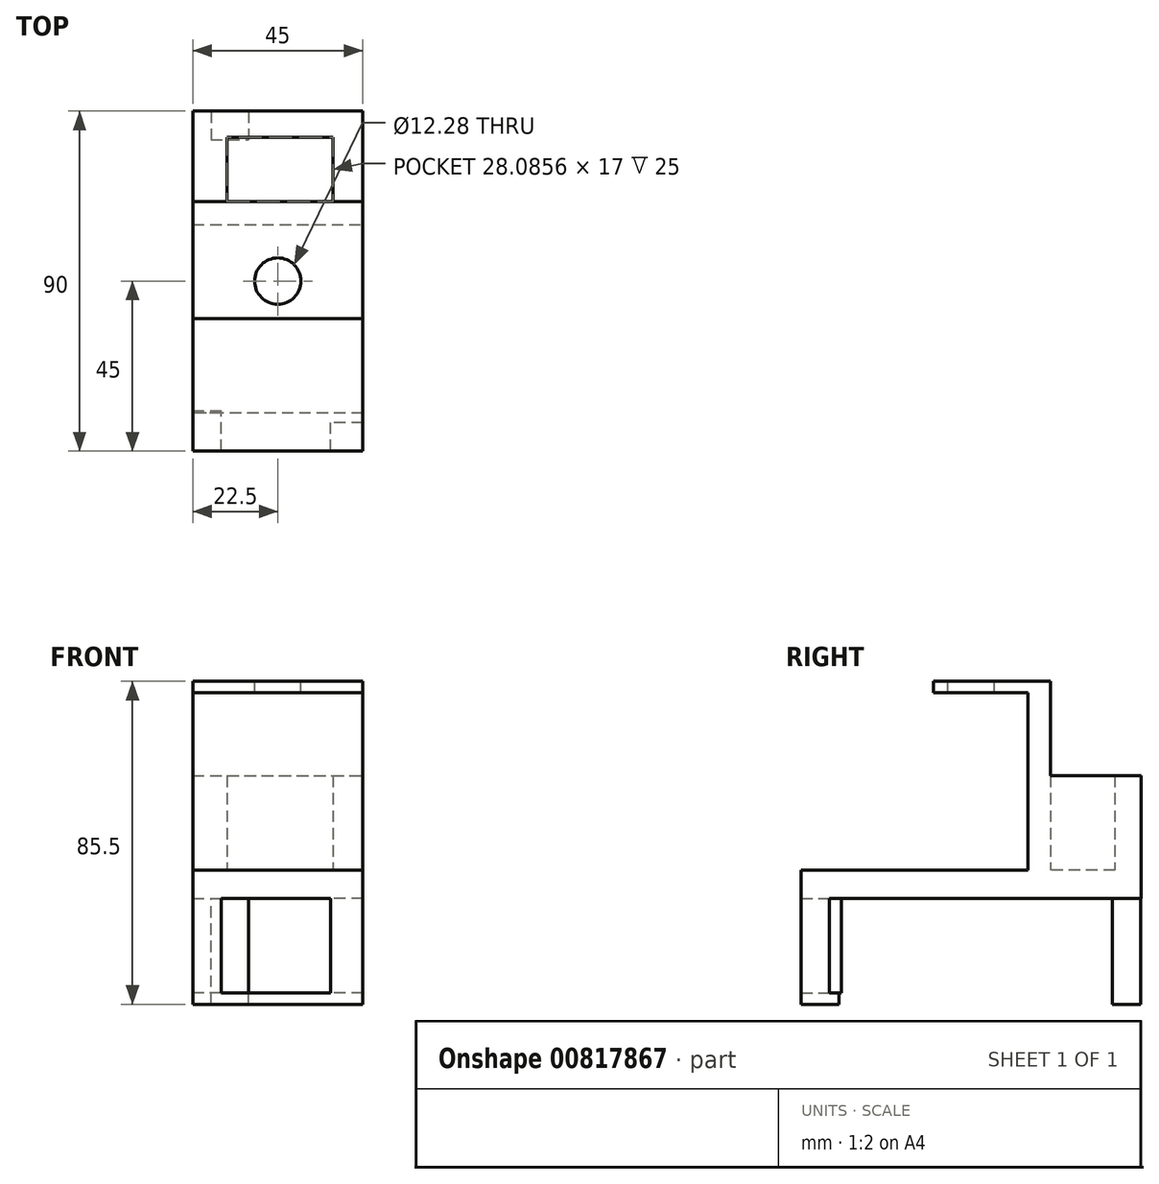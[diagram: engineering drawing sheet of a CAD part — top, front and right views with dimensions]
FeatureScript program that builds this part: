
annotation { "Feature Type Name" : "Feature", "Feature Type Description" : "" }
export const myFeature = defineFeature(function(context is Context, id is Id, definition is map)
    precondition{}
    {
        {
            var Q0;
            Q0=qCreatedBy(makeId("Top.planeOp"),FACE);
            var sketch = newSketch(context, id + "F0", { "sketchPlane" : qUnion([Q0])});
            skLineSegment(sketch, "E0.bottom", {"start": v(-22.5, 45) * mm, "end": v(22.5, 45) * mm});
            skLineSegment(sketch, "E0.top", {"start": v(-22.5, -45) * mm, "end": v(22.5, -45) * mm});
            skLineSegment(sketch, "E0.left", {"start": v(-22.5, 45) * mm, "end": v(-22.5, -45) * mm});
            skLineSegment(sketch, "E0.right", {"start": v(22.5, 45) * mm, "end": v(22.5, -45) * mm});
            skPoint(sketch, "E0.middle", {"position": v(0, 0) * mm});
            skSolve(sketch);
        }
        {
            var Q0;
            Q0=makeQuery(id+"F0.imprint","IMPRINT",FACE,{"disambiguationData":[TD([[makeQuery(id+"F0.imprint","IMPRINT",EDGE,{"derivedFrom":sQuery(id+"F0.wireOp",EDGE,"E0.bottom")}),-1.0]])]});
            extrude(context, id + "F1", {"entities" : qUnion([Q0]), "depth" : 7.5 * mm, "offsetDistance" : 25 * mm});
        }
        {
            var Q0;
            Q0=makeQuery(id+"F1.opExtrude","CAP_FACE",FACE,{"disambiguationData":[OSD([sQuery(id+"F0.wireOp",EDGE,"E0.bottom"),sQuery(id+"F0.wireOp",EDGE,"E0.top"),sQuery(id+"F0.wireOp",EDGE,"E0.left"),sQuery(id+"F0.wireOp",EDGE,"E0.right")])],"isStart":false});
            var sketch = newSketch(context, id + "F2", { "sketchPlane" : qUnion([Q0])});
            skLineSegment(sketch, "E1.bottom", {"start": v(-22.5, 45) * mm, "end": v(22.5, 45) * mm});
            skLineSegment(sketch, "E1.top", {"start": v(-22.5, 15) * mm, "end": v(22.5, 15) * mm});
            skLineSegment(sketch, "E1.left", {"start": v(-22.5, 45) * mm, "end": v(-22.5, 15) * mm});
            skLineSegment(sketch, "E1.right", {"start": v(22.5, 45) * mm, "end": v(22.5, 15) * mm});
            skLineSegment(sketch, "E2.bottom", {"start": v(-13.5, 38.06) * mm, "end": v(14.6, 38.06) * mm});
            skLineSegment(sketch, "E2.top", {"start": v(-13.5, 21.06) * mm, "end": v(14.6, 21.06) * mm});
            skLineSegment(sketch, "E2.left", {"start": v(-13.5, 38.06) * mm, "end": v(-13.5, 21.06) * mm});
            skLineSegment(sketch, "E2.right", {"start": v(14.6, 38.06) * mm, "end": v(14.6, 21.06) * mm});
            skSolve(sketch);
        }
        {
            var Q0;
            Q0=makeQuery(id+"F2.imprint","IMPRINT",FACE,{"disambiguationData":[TD([[makeQuery(id+"F2.imprint","IMPRINT",EDGE,{"derivedFrom":sQuery(id+"F2.wireOp",EDGE,"E1.bottom")}),-1.0]])]});
            extrude(context, id + "F3", {"entities" : qUnion([Q0]), "operationType" : NewBodyOperationType.ADD, "depth" : 25 * mm, "offsetDistance" : 25 * mm});
        }
        {
            var Q0;
            Q0=makeQuery(id+"F3.opExtrude","CAP_FACE",FACE,{"disambiguationData":[OSD([sQuery(id+"F2.wireOp",EDGE,"E1.bottom"),sQuery(id+"F2.wireOp",EDGE,"E1.top"),sQuery(id+"F2.wireOp",EDGE,"E1.left"),sQuery(id+"F2.wireOp",EDGE,"E1.right"),sQuery(id+"F2.wireOp",EDGE,"E2.bottom"),sQuery(id+"F2.wireOp",EDGE,"E2.top"),sQuery(id+"F2.wireOp",EDGE,"E2.left"),sQuery(id+"F2.wireOp",EDGE,"E2.right")])],"isStart":false});
            var sketch = newSketch(context, id + "F4", { "sketchPlane" : qUnion([Q0])});
            skLineSegment(sketch, "E3.bottom", {"start": v(22.5, 15) * mm, "end": v(-22.5, 15) * mm});
            skLineSegment(sketch, "E3.top", {"start": v(22.5, 21.06) * mm, "end": v(-22.5, 21.06) * mm});
            skLineSegment(sketch, "E3.left", {"start": v(22.5, 15) * mm, "end": v(22.5, 21.06) * mm});
            skLineSegment(sketch, "E3.right", {"start": v(-22.5, 15) * mm, "end": v(-22.5, 21.06) * mm});
            skSolve(sketch);
        }
        {
            var Q0;
            Q0=makeQuery(id+"F4.imprint","IMPRINT",FACE,{"disambiguationData":[TD([[makeQuery(id+"F4.imprint","IMPRINT",EDGE,{"derivedFrom":sQuery(id+"F4.wireOp",EDGE,"E3.bottom")}),1.0]])]});
            extrude(context, id + "F5", {"entities" : qUnion([Q0]), "operationType" : NewBodyOperationType.ADD, "depth" : 25 * mm, "offsetDistance" : 25 * mm});
        }
        {
            var Q0;
            Q0=makeQuery(id+"F5.boolean.opBoolean","MERGE",FACE,{"derivedFrom":[makeQuery(id+"F3.opExtrude","SWEPT_FACE",FACE,{"disambiguationData":[OSD([sQuery(id+"F2.wireOp",EDGE,"E1.top")])]}),makeQuery(id+"F5.opExtrude","SWEPT_FACE",FACE,{"disambiguationData":[OSD([sQuery(id+"F4.wireOp",EDGE,"E3.bottom")])]})]});
            var sketch = newSketch(context, id + "F6", { "sketchPlane" : qUnion([Q0])});
            skLineSegment(sketch, "E4.bottom", {"start": v(-22.5, 57.5) * mm, "end": v(22.5, 57.5) * mm});
            skLineSegment(sketch, "E4.top", {"start": v(-22.5, 54.5) * mm, "end": v(22.5, 54.5) * mm});
            skLineSegment(sketch, "E4.left", {"start": v(-22.5, 57.5) * mm, "end": v(-22.5, 54.5) * mm});
            skLineSegment(sketch, "E4.right", {"start": v(22.5, 57.5) * mm, "end": v(22.5, 54.5) * mm});
            skSolve(sketch);
        }
        {
            var Q0;
            Q0=makeQuery(id+"F6.imprint","IMPRINT",FACE,{"disambiguationData":[TD([[makeQuery(id+"F6.imprint","IMPRINT",EDGE,{"derivedFrom":sQuery(id+"F6.wireOp",EDGE,"E4.bottom")}),-1.0]])]});
            extrude(context, id + "F7", {"entities" : qUnion([Q0]), "operationType" : NewBodyOperationType.ADD, "depth" : 25 * mm, "offsetDistance" : 25 * mm});
        }
        {
            var Q0;
            Q0=makeQuery(id+"F7.boolean.opBoolean","MERGE",FACE,{"derivedFrom":[makeQuery(id+"F5.opExtrude","CAP_FACE",FACE,{"disambiguationData":[OSD([sQuery(id+"F4.wireOp",EDGE,"E3.bottom"),sQuery(id+"F4.wireOp",EDGE,"E3.top"),sQuery(id+"F4.wireOp",EDGE,"E3.left"),sQuery(id+"F4.wireOp",EDGE,"E3.right")])],"isStart":false}),makeQuery(id+"F7.opExtrude","SWEPT_FACE",FACE,{"disambiguationData":[OSD([sQuery(id+"F6.wireOp",EDGE,"E4.bottom")])]})]});
            var sketch = newSketch(context, id + "F8", { "sketchPlane" : qUnion([Q0])});
            skCircle(sketch, "E5", {"center": v(0, 0) * mm, "radius": 6.14 * mm});
            skSolve(sketch);
        }
        {
            var Q0;
            Q0=makeQuery(id+"F8.imprint","IMPRINT",FACE,{"disambiguationData":[TD([[makeQuery(id+"F8.imprint","IMPRINT",EDGE,{"derivedFrom":sQuery(id+"F8.wireOp",EDGE,"E5")}),1.0]])]});
            var Q1;
            Q1=sQuery(id+"F8.wireOp",EDGE,"E5");
            extrude(context, id + "F9", {"entities" : qUnion([Q0]), "operationType" : NewBodyOperationType.REMOVE, "surfaceEntities" : qUnion([Q1]), "endBound" : BoundingType.UP_TO_NEXT, "oppositeDirection" : true, "depth" : 25 * mm, "offsetDistance" : 25 * mm});
        }
        {
            var Q0;
            Q0=makeQuery(id+"F1.opExtrude","CAP_FACE",FACE,{"disambiguationData":[OSD([sQuery(id+"F0.wireOp",EDGE,"E0.bottom"),sQuery(id+"F0.wireOp",EDGE,"E0.top"),sQuery(id+"F0.wireOp",EDGE,"E0.left"),sQuery(id+"F0.wireOp",EDGE,"E0.right")])],"isStart":true});
            var sketch = newSketch(context, id + "F10", { "sketchPlane" : qUnion([Q0])});
            skLineSegment(sketch, "E6.bottom", {"start": v(22.5, 45) * mm, "end": v(14, 45) * mm});
            skLineSegment(sketch, "E6.top", {"start": v(22.5, 37.5) * mm, "end": v(14, 37.5) * mm});
            skLineSegment(sketch, "E6.left", {"start": v(22.5, 45) * mm, "end": v(22.5, 37.5) * mm});
            skLineSegment(sketch, "E6.right", {"start": v(14, 45) * mm, "end": v(14, 37.5) * mm});
            skSolve(sketch);
        }
        {
            var Q0;
            Q0=makeQuery(id+"F10.imprint","IMPRINT",FACE,{"disambiguationData":[TD([[makeQuery(id+"F10.imprint","IMPRINT",EDGE,{"derivedFrom":sQuery(id+"F10.wireOp",EDGE,"E6.bottom")}),-1.0]])]});
            extrude(context, id + "F11", {"entities" : qUnion([Q0]), "operationType" : NewBodyOperationType.ADD, "depth" : 25 * mm, "offsetDistance" : 25 * mm});
        }
        {
            var Q0;
            Q0=makeQuery(id+"F1.opExtrude","CAP_FACE",FACE,{"disambiguationData":[OSD([sQuery(id+"F0.wireOp",EDGE,"E0.bottom"),sQuery(id+"F0.wireOp",EDGE,"E0.top"),sQuery(id+"F0.wireOp",EDGE,"E0.left"),sQuery(id+"F0.wireOp",EDGE,"E0.right")])],"isStart":true});
            var sketch = newSketch(context, id + "F12", { "sketchPlane" : qUnion([Q0])});
            skLineSegment(sketch, "E7.bottom", {"start": v(-22.5, 45) * mm, "end": v(-15, 45) * mm});
            skLineSegment(sketch, "E7.top", {"start": v(-22.5, 34.34) * mm, "end": v(-15, 34.34) * mm});
            skLineSegment(sketch, "E7.left", {"start": v(-22.5, 45) * mm, "end": v(-22.5, 34.34) * mm});
            skLineSegment(sketch, "E7.right", {"start": v(-15, 45) * mm, "end": v(-15, 34.34) * mm});
            skSolve(sketch);
        }
        {
            var Q0;
            Q0=makeQuery(id+"F12.imprint","IMPRINT",FACE,{"disambiguationData":[TD([[makeQuery(id+"F12.imprint","IMPRINT",EDGE,{"derivedFrom":sQuery(id+"F12.wireOp",EDGE,"E7.bottom")}),-1.0]])]});
            extrude(context, id + "F13", {"entities" : qUnion([Q0]), "operationType" : NewBodyOperationType.ADD, "depth" : 25 * mm, "offsetDistance" : 25 * mm});
        }
        {
            var Q0;
            Q0=qCreatedBy(makeId("Top.planeOp"),FACE);
            var sketch = newSketch(context, id + "F14", { "sketchPlane" : qUnion([Q0])});
            skLineSegment(sketch, "E8.bottom", {"start": v(-17.7, 44.93) * mm, "end": v(-7.7, 44.93) * mm});
            skLineSegment(sketch, "E8.top", {"start": v(-17.7, 37.43) * mm, "end": v(-7.7, 37.43) * mm});
            skLineSegment(sketch, "E8.left", {"start": v(-17.7, 44.93) * mm, "end": v(-17.7, 37.43) * mm});
            skLineSegment(sketch, "E8.right", {"start": v(-7.7, 44.93) * mm, "end": v(-7.7, 37.43) * mm});
            skSolve(sketch);
        }
        {
            var Q0;
            Q0=makeQuery(id+"F14.imprint","IMPRINT",FACE,{"disambiguationData":[TD([[makeQuery(id+"F14.imprint","IMPRINT",EDGE,{"derivedFrom":sQuery(id+"F14.wireOp",EDGE,"E8.bottom")}),-1.0]])]});
            extrude(context, id + "F15", {"entities" : qUnion([Q0]), "operationType" : NewBodyOperationType.ADD, "depth" : -28 * mm, "offsetDistance" : 25 * mm});
        }
        {
            var Q0;
            Q0=makeQuery(id+"F11.opExtrude","CAP_FACE",FACE,{"disambiguationData":[OSD([sQuery(id+"F10.wireOp",EDGE,"E6.bottom"),sQuery(id+"F10.wireOp",EDGE,"E6.top"),sQuery(id+"F10.wireOp",EDGE,"E6.left"),sQuery(id+"F10.wireOp",EDGE,"E6.right")])],"isStart":false});
            var sketch = newSketch(context, id + "F16", { "sketchPlane" : qUnion([Q0])});
            skLineSegment(sketch, "E9.bottom", {"start": v(22.5, 45) * mm, "end": v(-22.5, 45) * mm});
            skLineSegment(sketch, "E9.top", {"start": v(22.5, 35) * mm, "end": v(-22.5, 35) * mm});
            skLineSegment(sketch, "E9.left", {"start": v(22.5, 45) * mm, "end": v(22.5, 35) * mm});
            skLineSegment(sketch, "E9.right", {"start": v(-22.5, 45) * mm, "end": v(-22.5, 35) * mm});
            skSolve(sketch);
        }
        {
            var Q0;
            Q0 = qSketchRegion(id + "F16", true);
            extrude(context, id + "F17", {"entities" : qUnion([Q0]), "operationType" : NewBodyOperationType.ADD, "depth" : 3 * mm, "offsetDistance" : 25 * mm});
        }
    });
